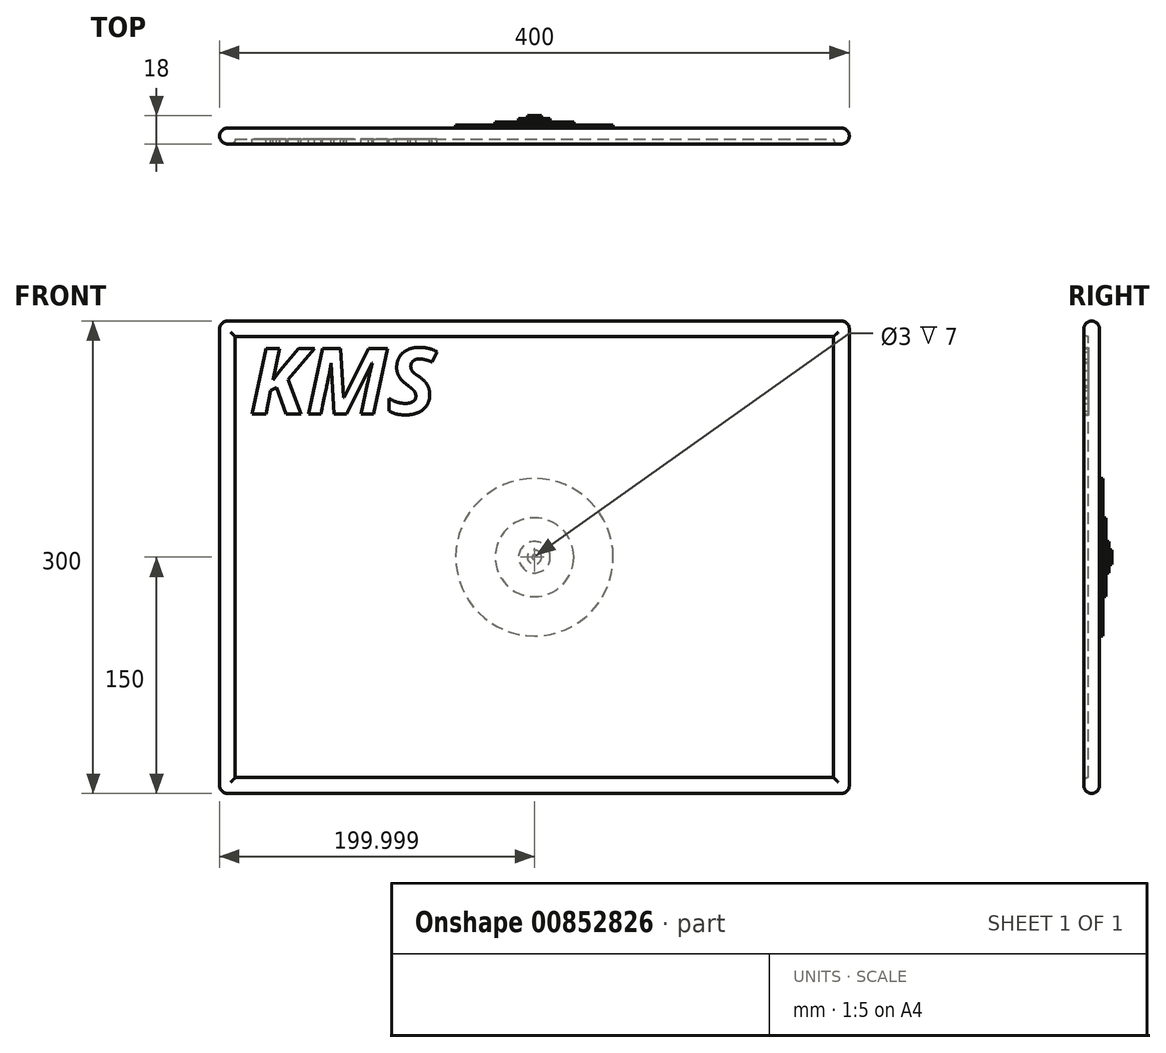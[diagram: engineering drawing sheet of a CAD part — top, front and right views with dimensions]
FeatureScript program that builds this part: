
annotation { "Feature Type Name" : "Feature", "Feature Type Description" : "" }
export const myFeature = defineFeature(function(context is Context, id is Id, definition is map)
    precondition{}
    {
        {
            var Q0;
            Q0=qCreatedBy(makeId("Front.planeOp"),FACE);
            var sketch = newSketch(context, id + "F0", { "sketchPlane" : qUnion([Q0])});
            skLineSegment(sketch, "E0", {"start": v(-75.03, -40.2) * mm, "end": v(324.97, -40.2) * mm});
            skLineSegment(sketch, "E1", {"start": v(-75.03, -40.2) * mm, "end": v(-75.03, 259.8) * mm});
            skLineSegment(sketch, "E2", {"start": v(-75.03, 259.8) * mm, "end": v(324.97, 259.8) * mm});
            skLineSegment(sketch, "E3", {"start": v(324.97, 259.8) * mm, "end": v(324.97, -40.2) * mm});
            skLineSegment(sketch, "E4", {"start": v(-65.03, 249.8) * mm, "end": v(314.97, 249.8) * mm});
            skLineSegment(sketch, "E5", {"start": v(-65.03, -30.2) * mm, "end": v(-65.03, 249.8) * mm});
            skLineSegment(sketch, "E6", {"start": v(314.97, -30.2) * mm, "end": v(-65.03, -30.2) * mm});
            skLineSegment(sketch, "E7", {"start": v(314.97, -30.2) * mm, "end": v(314.97, 249.8) * mm});
            skLineSegment(sketch, "E8", {"start": v(324.97, 109.8) * mm, "end": v(124.97, 109.8) * mm, "construction": true});
            skLineSegment(sketch, "E9", {"start": v(124.97, -40.2) * mm, "end": v(124.97, 109.8) * mm, "construction": true});
            skSolve(sketch);
        }
        {
            var Q0;
            Q0=makeQuery(id+"F0.imprint","IMPRINT",FACE,{"disambiguationData":[TD([[makeQuery(id+"F0.imprint","IMPRINT",EDGE,{"derivedFrom":sQuery(id+"F0.wireOp",EDGE,"E0")}),1.0]])]});
            extrude(context, id + "F1", {"entities" : qUnion([Q0]), "depth" : 10 * mm, "offsetDistance" : 25 * mm});
        }
        {
            var Q0;
            Q0=makeQuery(id+"F0.imprint","IMPRINT",FACE,{"disambiguationData":[TD([[makeQuery(id+"F0.imprint","IMPRINT",EDGE,{"derivedFrom":sQuery(id+"F0.wireOp",EDGE,"E4")}),-1.0]])]});
            extrude(context, id + "F2", {"entities" : qUnion([Q0]), "operationType" : NewBodyOperationType.ADD, "depth" : 7 * mm, "offsetDistance" : 25 * mm});
        }
        {
            var Q0;
            Q0=makeQuery(id+"F1.opExtrude","CAP_EDGE",EDGE,{"disambiguationData":[OSD([sQuery(id+"F0.wireOp",EDGE,"E5")])],"isStart":false});
            fillet(context, id + "F3", {"entities" : qUnion([Q0]), "radius" : 3 * mm, "tangentPropagation" : true, "allowEdgeOverflow" : false});
        }
        {
            var Q0;
            Q0=makeQuery(id+"F1.opExtrude","CAP_EDGE",EDGE,{"disambiguationData":[OSD([sQuery(id+"F0.wireOp",EDGE,"E7")])],"isStart":false});
            fillet(context, id + "F4", {"entities" : qUnion([Q0]), "radius" : 3 * mm, "tangentPropagation" : true, "allowEdgeOverflow" : false});
        }
        {
            var Q0;
            Q0=makeQuery(id+"F1.opExtrude","CAP_EDGE",EDGE,{"disambiguationData":[OSD([sQuery(id+"F0.wireOp",EDGE,"E6")])],"isStart":false});
            fillet(context, id + "F5", {"entities" : qUnion([Q0]), "radius" : 3 * mm, "tangentPropagation" : true, "allowEdgeOverflow" : false});
        }
        {
            var Q0;
            Q0=makeQuery(id+"F1.opExtrude","CAP_EDGE",EDGE,{"disambiguationData":[OSD([sQuery(id+"F0.wireOp",EDGE,"E4")])],"isStart":false});
            fillet(context, id + "F6", {"entities" : qUnion([Q0]), "radius" : 3 * mm, "tangentPropagation" : true, "allowEdgeOverflow" : false});
        }
        {
            var Q0;
            Q0=makeQuery(id+"F1.opExtrude","SWEPT_EDGE",EDGE,{"disambiguationData":[OSD([sQuery(id+"F0.wireOp",EDGE,"E2"),sQuery(id+"F0.wireOp",EDGE,"E3")])]});
            var Q1;
            Q1=makeQuery(id+"F1.opExtrude","SWEPT_EDGE",EDGE,{"disambiguationData":[OSD([sQuery(id+"F0.wireOp",EDGE,"E0"),sQuery(id+"F0.wireOp",EDGE,"E3")])]});
            var Q2;
            Q2=makeQuery(id+"F1.opExtrude","SWEPT_EDGE",EDGE,{"disambiguationData":[OSD([sQuery(id+"F0.wireOp",EDGE,"E0"),sQuery(id+"F0.wireOp",EDGE,"E1")])]});
            var Q3;
            Q3=makeQuery(id+"F1.opExtrude","SWEPT_EDGE",EDGE,{"disambiguationData":[OSD([sQuery(id+"F0.wireOp",EDGE,"E1"),sQuery(id+"F0.wireOp",EDGE,"E2")])]});
            fillet(context, id + "F7", {"entities" : qUnion([Q0, Q1, Q2, Q3]), "radius" : 5 * mm, "tangentPropagation" : true, "allowEdgeOverflow" : false});
        }
        {
            var Q0;
            Q0=makeQuery(id+"F1.opExtrude","CAP_EDGE",EDGE,{"disambiguationData":[OSD([sQuery(id+"F0.wireOp",EDGE,"E1")])],"isStart":false});
            fillet(context, id + "F8", {"entities" : qUnion([Q0]), "radius" : 5 * mm, "tangentPropagation" : true, "allowEdgeOverflow" : false});
        }
        {
            var Q0;
            Q0=makeQuery(id+"F1.opExtrude","CAP_EDGE",EDGE,{"disambiguationData":[OSD([sQuery(id+"F0.wireOp",EDGE,"E1")])],"isStart":true});
            fillet(context, id + "F9", {"entities" : qUnion([Q0]), "radius" : 5 * mm, "tangentPropagation" : true, "allowEdgeOverflow" : false});
        }
        {
            var Q0;
            Q0=makeQuery(id+"F2.opExtrude","CAP_FACE",FACE,{"disambiguationData":[OSD([sQuery(id+"F0.wireOp",EDGE,"E4"),sQuery(id+"F0.wireOp",EDGE,"E5"),sQuery(id+"F0.wireOp",EDGE,"E6"),sQuery(id+"F0.wireOp",EDGE,"E7")])],"isStart":false});
            var sketch = newSketch(context, id + "F10", { "sketchPlane" : qUnion([Q0])});
            skText(sketch, "E10", { "text": "KMS", "fontName": "OpenSans-BoldItalic.ttf"});
            const initialGuessF10  = {"E10": [-0.05587, 0.20074, 1, 0, 0.04212]};
            skSetInitialGuess(sketch, initialGuessF10);
            skSolve(sketch);
        }
        {
            var Q0;
            Q0 = qSketchRegion(id + "F10", true);
            extrude(context, id + "F11", {"entities" : qUnion([Q0]), "operationType" : NewBodyOperationType.ADD, "depth" : 3 * mm, "offsetDistance" : 25 * mm});
        }
        {
            var Q0;
            Q0=makeQuery(id+"F0.imprint","IMPRINT",FACE,{"disambiguationData":[TD([[makeQuery(id+"F0.imprint","IMPRINT",EDGE,{"derivedFrom":sQuery(id+"F0.wireOp",EDGE,"E4")}),-1.0]])]});
            var sketch = newSketch(context, id + "F12", { "sketchPlane" : qUnion([Q0])});
            skCircle(sketch, "E11", {"center": v(124.97, 109.81) * mm, "radius": 50 * mm});
            skSolve(sketch);
        }
        {
            var Q0;
            Q0 = qSketchRegion(id + "F12", true);
            extrude(context, id + "F13", {"entities" : qUnion([Q0]), "operationType" : NewBodyOperationType.ADD, "oppositeDirection" : true, "depth" : 2 * mm, "offsetDistance" : 25 * mm});
        }
        {
            var Q0;
            Q0=makeQuery(id+"F13.opExtrude","CAP_FACE",FACE,{"disambiguationData":[OSD([sQuery(id+"F12.wireOp",EDGE,"E11")])],"isStart":false});
            var sketch = newSketch(context, id + "F14", { "sketchPlane" : qUnion([Q0])});
            skCircle(sketch, "E12", {"center": v(-124.97, 109.81) * mm, "radius": 25 * mm});
            skSolve(sketch);
        }
        {
            var Q0;
            Q0=makeQuery(id+"F14.imprint","IMPRINT",FACE,{"disambiguationData":[TD([[makeQuery(id+"F14.imprint","IMPRINT",EDGE,{"derivedFrom":sQuery(id+"F14.wireOp",EDGE,"E12")}),1.0]])]});
            extrude(context, id + "F15", {"entities" : qUnion([Q0]), "operationType" : NewBodyOperationType.ADD, "depth" : 2 * mm, "offsetDistance" : 25 * mm});
        }
        {
            var Q0;
            Q0=makeQuery(id+"F15.opExtrude","CAP_FACE",FACE,{"disambiguationData":[OSD([sQuery(id+"F14.wireOp",EDGE,"E12")])],"isStart":false});
            var sketch = newSketch(context, id + "F16", { "sketchPlane" : qUnion([Q0])});
            skCircle(sketch, "E13", {"center": v(-124.97, 109.81) * mm, "radius": 10 * mm});
            skSolve(sketch);
        }
        {
            var Q0;
            Q0 = qSketchRegion(id + "F16", true);
            extrude(context, id + "F17", {"entities" : qUnion([Q0]), "operationType" : NewBodyOperationType.ADD, "depth" : 2 * mm, "offsetDistance" : 25 * mm});
        }
        {
            var Q0;
            Q0=makeQuery(id+"F17.opExtrude","CAP_FACE",FACE,{"disambiguationData":[OSD([sQuery(id+"F16.wireOp",EDGE,"E13")])],"isStart":false});
            var sketch = newSketch(context, id + "F18", { "sketchPlane" : qUnion([Q0])});
            skCircle(sketch, "E14", {"center": v(-124.97, 109.81) * mm, "radius": 4.5 * mm});
            skSolve(sketch);
        }
        {
            var Q0;
            Q0=makeQuery(id+"F18.imprint","IMPRINT",FACE,{"disambiguationData":[TD([[makeQuery(id+"F18.imprint","IMPRINT",EDGE,{"derivedFrom":sQuery(id+"F18.wireOp",EDGE,"E14")}),1.0]])]});
            extrude(context, id + "F19", {"entities" : qUnion([Q0]), "operationType" : NewBodyOperationType.ADD, "depth" : 2 * mm, "offsetDistance" : 25 * mm});
        }
        {
            var Q0;
            Q0=makeQuery(id+"F19.opExtrude","CAP_FACE",FACE,{"disambiguationData":[OSD([sQuery(id+"F18.wireOp",EDGE,"E14")])],"isStart":false});
            var sketch = newSketch(context, id + "F20", { "sketchPlane" : qUnion([Q0])});
            skCircle(sketch, "E15", {"center": v(-124.97, 109.81) * mm, "radius": 1.5 * mm});
            skSolve(sketch);
        }
        {
            var Q0;
            Q0 = qSketchRegion(id + "F20", true);
            extrude(context, id + "F21", {"entities" : qUnion([Q0]), "operationType" : NewBodyOperationType.REMOVE, "oppositeDirection" : true, "depth" : 7 * mm, "offsetDistance" : 25 * mm});
        }
    });
